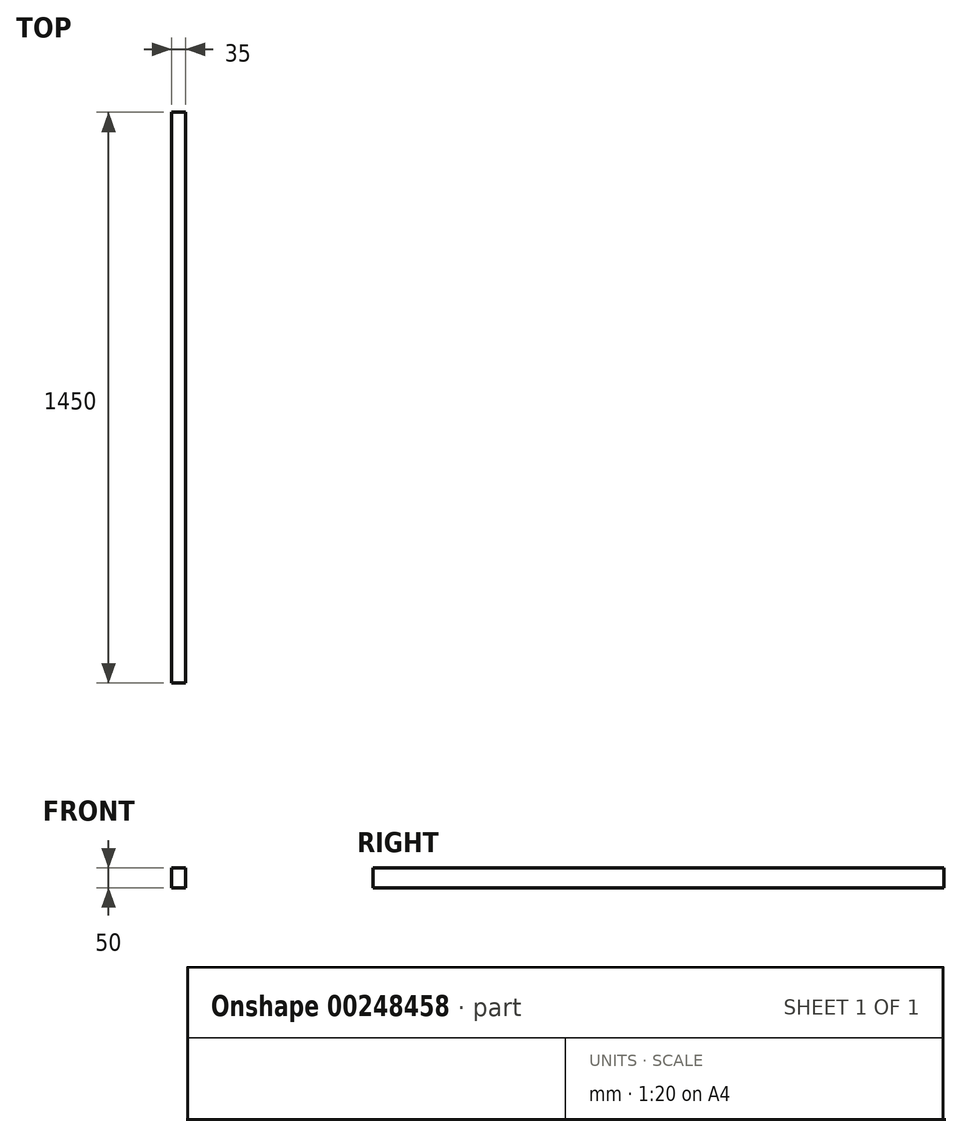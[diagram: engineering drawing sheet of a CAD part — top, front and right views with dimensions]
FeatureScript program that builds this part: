
annotation { "Feature Type Name" : "Feature", "Feature Type Description" : "" }
export const myFeature = defineFeature(function(context is Context, id is Id, definition is map)
    precondition{}
    {
        {
            var Q0;
            Q0=qCreatedBy(makeId("Top.planeOp"),FACE);
            var sketch = newSketch(context, id + "F0", { "sketchPlane" : qUnion([Q0])});
            skLineSegment(sketch, "E0.bottom", {"start": v(34.37, -725) * mm, "end": v(69.37, -725) * mm});
            skLineSegment(sketch, "E0.top", {"start": v(34.37, 725) * mm, "end": v(69.37, 725) * mm});
            skLineSegment(sketch, "E0.left", {"start": v(34.37, -725) * mm, "end": v(34.37, 725) * mm});
            skLineSegment(sketch, "E0.right", {"start": v(69.37, -725) * mm, "end": v(69.37, 725) * mm});
            skSolve(sketch);
        }
        {
            var Q0;
            Q0 = qSketchRegion(id + "F0", true);
            extrude(context, id + "F1", {"entities" : qUnion([Q0]), "depth" : 50 * mm});
        }
    });
